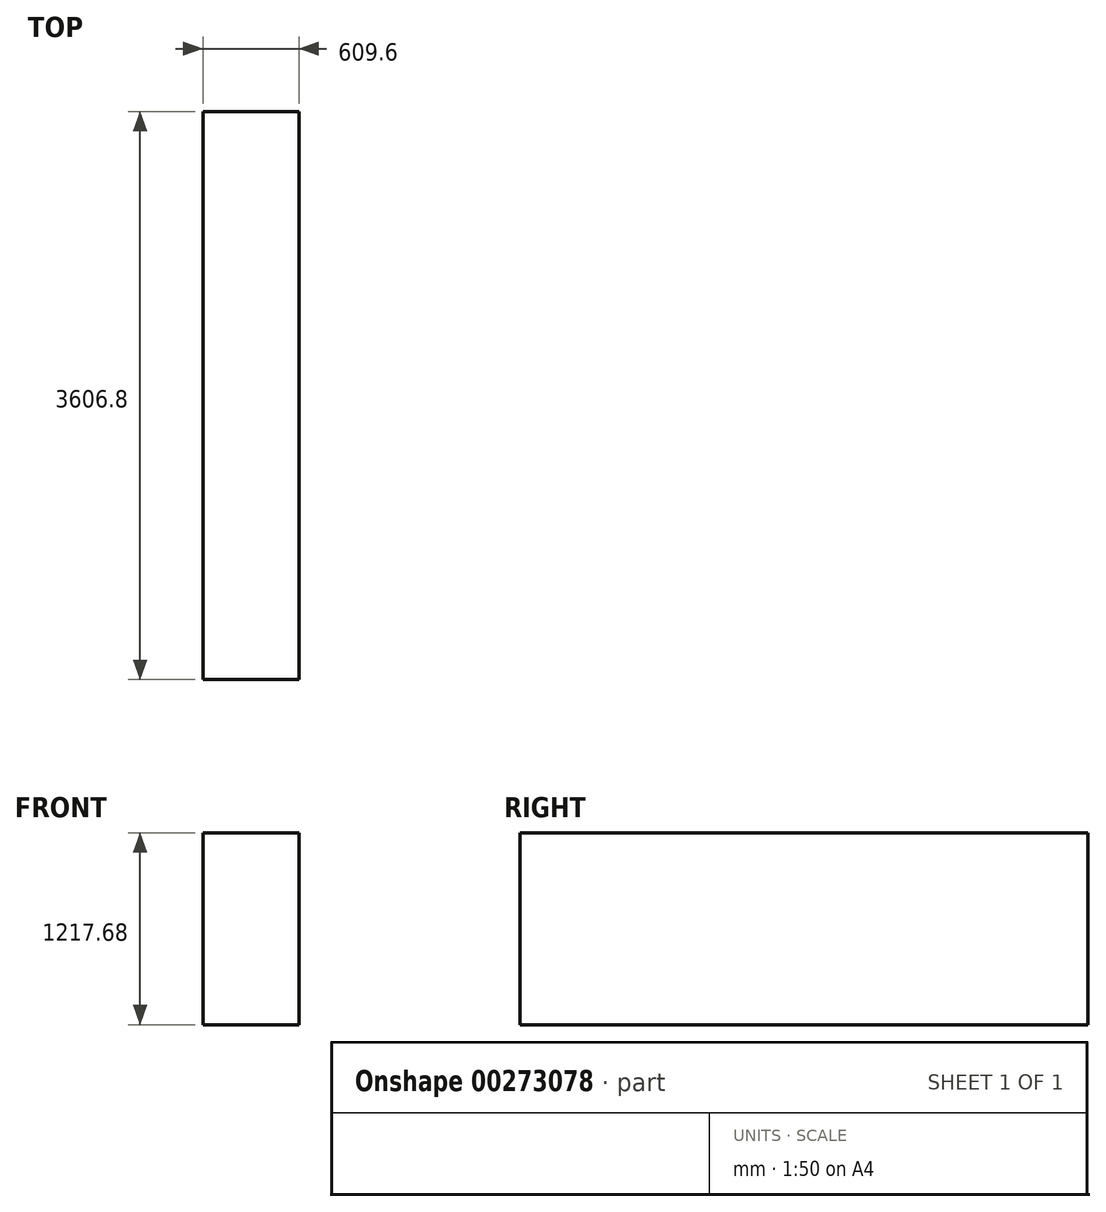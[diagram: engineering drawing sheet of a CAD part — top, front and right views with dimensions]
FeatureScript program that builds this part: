
annotation { "Feature Type Name" : "Feature", "Feature Type Description" : "" }
export const myFeature = defineFeature(function(context is Context, id is Id, definition is map)
    precondition{}
    {
        {
            var Q0;
            Q0=qCreatedBy(makeId("Right.planeOp"),FACE);
            var sketch = newSketch(context, id + "F0", { "sketchPlane" : qUnion([Q0])});
            skLineSegment(sketch, "E0.bottom", {"start": v(1825.34, 623.42) * mm, "end": v(-1781.46, 623.42) * mm});
            skLineSegment(sketch, "E0.top", {"start": v(1825.34, -594.26) * mm, "end": v(-1781.46, -594.26) * mm});
            skLineSegment(sketch, "E0.left", {"start": v(1825.34, 623.42) * mm, "end": v(1825.34, -594.26) * mm});
            skLineSegment(sketch, "E0.right", {"start": v(-1781.46, 623.42) * mm, "end": v(-1781.46, -594.26) * mm});
            skSolve(sketch);
        }
        {
            var Q0;
            Q0 = qSketchRegion(id + "F0", true);
            extrude(context, id + "F1", {"entities" : qUnion([Q0]), "depth" : 609.6 * mm});
        }
    });
